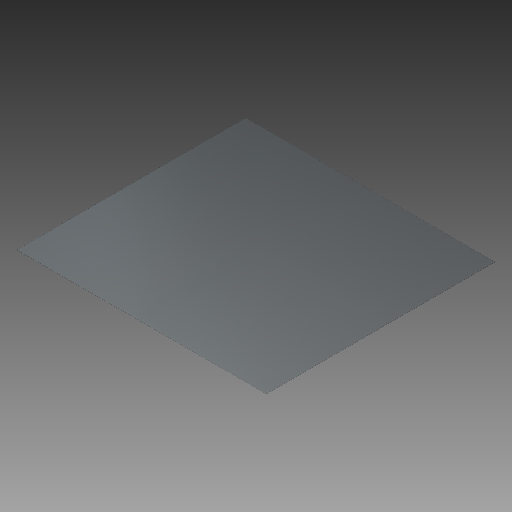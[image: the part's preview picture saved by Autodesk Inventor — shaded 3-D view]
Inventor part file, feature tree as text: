
AUTODESK INVENTOR PART (.ipt)
format: ipt  version: 2018 (Build 220112000, 112)  size: 93,696 bytes
history: native  units: mm
features: extrude x1, sketch x1
ambient origin geometry x8: Origin, YZ Plane, XZ Plane, XY Plane, X Axis, Y Axis, Z Axis, Center Point
bodies: Volumenkörper1 (feature_tree)
feature tree (2):
  extrude  "Extrusion1"  Depth=550.0mm
  sketch  "Skizze1"  dims[d0=600.0mm d1=550.0mm d2=300.0mm d3=275.0mm d4=0.8mm d5=0.0mm]
